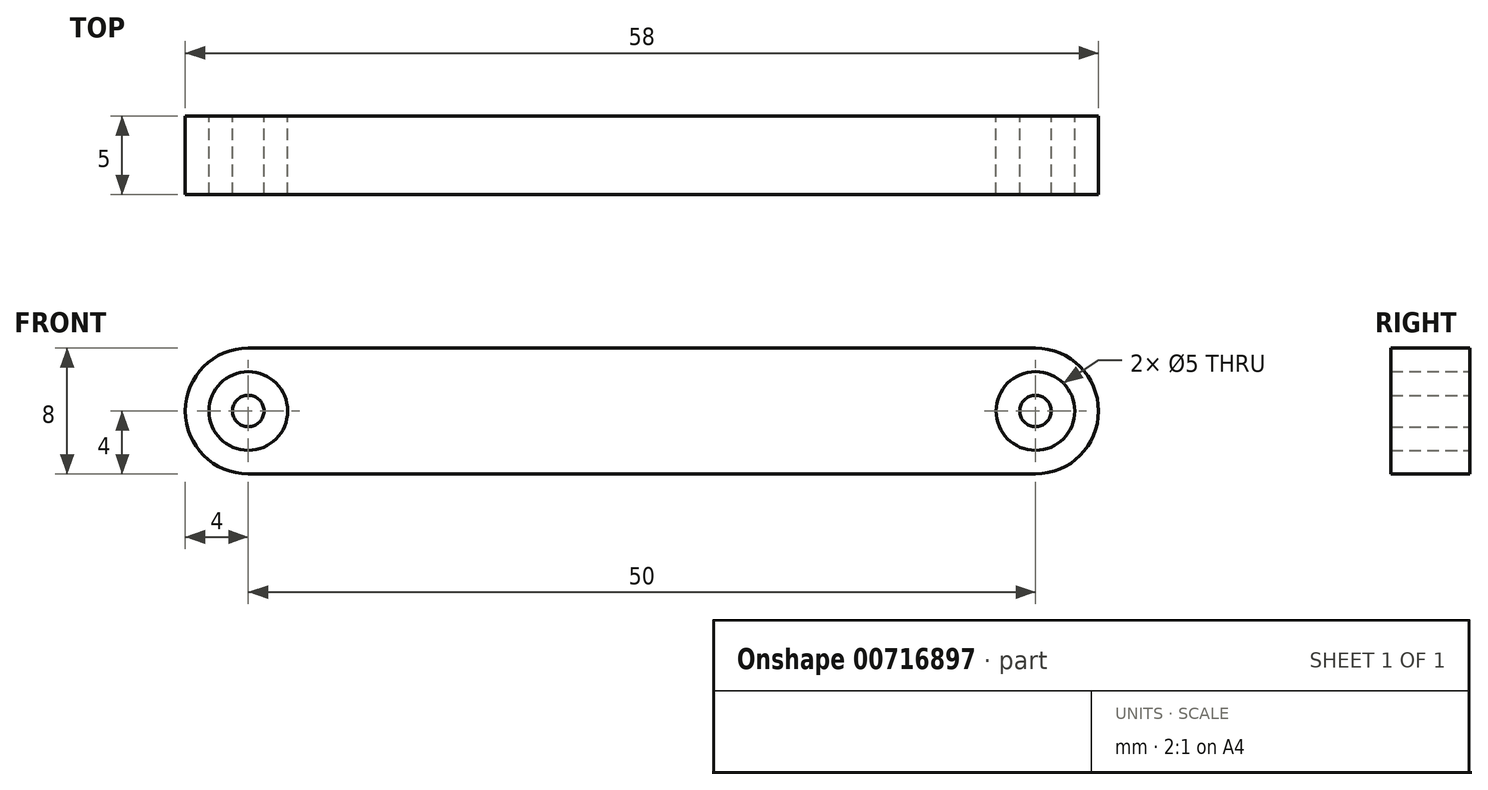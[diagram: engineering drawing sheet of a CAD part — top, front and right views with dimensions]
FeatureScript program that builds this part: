
annotation { "Feature Type Name" : "Feature", "Feature Type Description" : "" }
export const myFeature = defineFeature(function(context is Context, id is Id, definition is map)
    precondition{}
    {
        {
            var Q0;
            Q0=qCreatedBy(makeId("Front.planeOp"),FACE);
            var sketch = newSketch(context, id + "F0", { "sketchPlane" : qUnion([Q0])});
            skArc(sketch, "E0", {"start": v(0, -4) * mm, "mid": v(4, 0) * mm, "end": v(0, 4) * mm});
            skArc(sketch, "E1", {"start": v(-50, 4) * mm, "mid": v(-54, 0) * mm, "end": v(-50, -4) * mm});
            skLineSegment(sketch, "E2", {"start": v(0, 4) * mm, "end": v(-50, 4) * mm});
            skLineSegment(sketch, "E3", {"start": v(0, -4) * mm, "end": v(-50, -4) * mm});
            skCircle(sketch, "E4", {"center": v(-50, 0) * mm, "radius": 2.5 * mm});
            skCircle(sketch, "E5", {"center": v(0, 0) * mm, "radius": 2.5 * mm});
            skCircle(sketch, "E6", {"center": v(-50, 0) * mm, "radius": 1 * mm});
            skCircle(sketch, "E7", {"center": v(0, 0) * mm, "radius": 1 * mm});
            skSolve(sketch);
        }
        {
            var Q0;
            Q0 = qSketchRegion(id + "F0", true);
            var Q1;
            Q1=makeQuery(id+"F0.imprint","IMPRINT",FACE,{"disambiguationData":[TD([[makeQuery(id+"F0.imprint","IMPRINT",EDGE,{"derivedFrom":sQuery(id+"F0.wireOp",EDGE,"E6")}),1.0]])]});
            var Q2;
            Q2=makeQuery(id+"F0.imprint","IMPRINT",FACE,{"disambiguationData":[TD([[makeQuery(id+"F0.imprint","IMPRINT",EDGE,{"derivedFrom":sQuery(id+"F0.wireOp",EDGE,"E7")}),1.0]])]});
            extrude(context, id + "F1", {"entities" : qUnion([Q0, Q1, Q2]), "depth" : 5 * mm, "offsetDistance" : 25.4 * mm});
        }
    });
